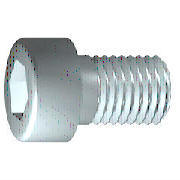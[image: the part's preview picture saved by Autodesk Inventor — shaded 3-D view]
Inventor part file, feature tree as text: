
AUTODESK INVENTOR PART (.ipt)
format: ipt  version: 2024.1 (Build 281209000, 209)  size: 187,392 bytes
history: native  units: mm (DEFAULTED — no unit token found)
features: extrude x1, plane x1, fillet x1
ambient origin geometry x7: Origin, YZ Plane, XY Plane, X Axis, Y Axis, Z Axis, Center Point
bodies: Solid1 (feature_tree), Body (feature_tree)
feature tree (3):
  extrude  "Slot"  Depth=18.75mm
  plane  "Work Plane1"
  fillet  "Fillet2"  Radius=0.306825mm
